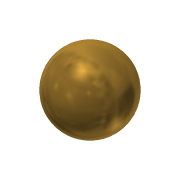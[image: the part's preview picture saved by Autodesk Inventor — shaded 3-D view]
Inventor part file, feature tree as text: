
AUTODESK INVENTOR PART (.ipt)
format: ipt  version: 2016 (Build 200138000, 138)  size: 99,840 bytes
history: native  units: mm
features: revolve x1, sketch x1
ambient origin geometry x8: Origin, YZ Plane, XZ Plane, XY Plane, X Axis, Y Axis, Z Axis, Center Point
bodies: Solid1 (feature_tree)
feature tree (2):
  revolve  "Revolution1"  [1 undecoded]
  sketch  "Sketch1"  dims[d0=90.0deg]
note: 1 required parameter value undecoded (feature->parameter linkage not recoverable at this tier; creation-order binding heuristic only, values carry confidence <= 0.55)
